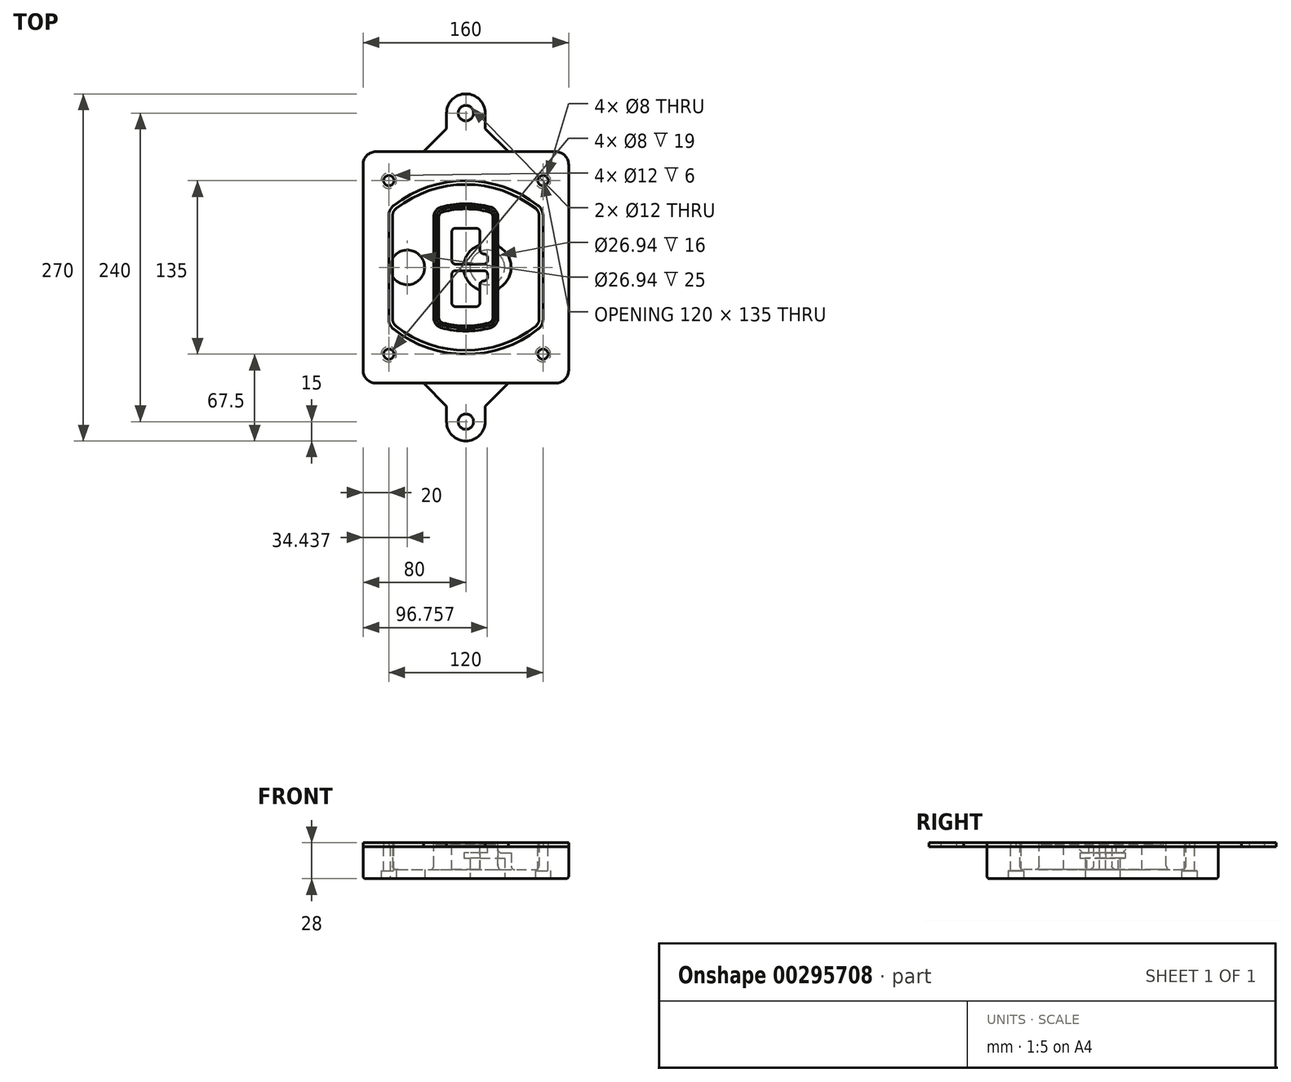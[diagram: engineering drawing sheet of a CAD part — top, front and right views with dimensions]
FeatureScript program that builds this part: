
annotation { "Feature Type Name" : "Feature", "Feature Type Description" : "" }
export const myFeature = defineFeature(function(context is Context, id is Id, definition is map)
    precondition{}
    {
        {
            var Q0;
            Q0=qCreatedBy(makeId("Top.planeOp"),FACE);
            var sketch = newSketch(context, id + "F0", { "sketchPlane" : qUnion([Q0])});
            skPoint(sketch, "E0.rect.middle", {"position": v(0, 0) * mm});
            skLineSegment(sketch, "E1.bottom", {"start": v(-70, -90) * mm, "end": v(70, -90) * mm});
            skLineSegment(sketch, "E1.top", {"start": v(-70, 90) * mm, "end": v(70, 90) * mm});
            skLineSegment(sketch, "E1.left", {"start": v(-80, -80) * mm, "end": v(-80, 80) * mm});
            skLineSegment(sketch, "E1.right", {"start": v(80, -80) * mm, "end": v(80, 80) * mm});
            skLineSegment(sketch, "E2", {"start": v(-80, 90) * mm, "end": v(80, -90) * mm, "construction": true});
            skLineSegment(sketch, "E3", {"start": v(80, 90) * mm, "end": v(-80, -90) * mm, "construction": true});
            skCircle(sketch, "E4", {"center": v(-60, 67.5) * mm, "radius": 4 * mm});
            skCircle(sketch, "E5", {"center": v(60, 67.5) * mm, "radius": 4 * mm});
            skCircle(sketch, "E6", {"center": v(60, -67.5) * mm, "radius": 4 * mm});
            skCircle(sketch, "E7", {"center": v(-60, -67.5) * mm, "radius": 4 * mm});
            skLineSegment(sketch, "E8", {"start": v(-60, 67.5) * mm, "end": v(60, 67.5) * mm, "construction": true});
            skLineSegment(sketch, "E9", {"start": v(60, 67.5) * mm, "end": v(60, -67.5) * mm, "construction": true});
            skLineSegment(sketch, "E10", {"start": v(60, -67.5) * mm, "end": v(-60, -67.5) * mm, "construction": true});
            skLineSegment(sketch, "E11", {"start": v(-60, -67.5) * mm, "end": v(-60, 67.5) * mm, "construction": true});
            skLineSegment(sketch, "E12", {"start": v(-60, 40.3) * mm, "end": v(-60, -40.3) * mm});
            skLineSegment(sketch, "E13", {"start": v(60, 40.3) * mm, "end": v(60, -40.3) * mm});
            skArc(sketch, "E14", {"start": v(56.15, 48.18) * mm, "mid": v(0, 67.5) * mm, "end": v(-56.15, 48.18) * mm});
            skArc(sketch, "E15", {"start": v(-56.15, -48.18) * mm, "mid": v(0, -67.5) * mm, "end": v(56.15, -48.18) * mm});
            skLineSegment(sketch, "E16", {"start": v(-60, 0) * mm, "end": v(60, 0) * mm, "construction": true});
            skPoint(sketch, "E17.visualSharp", {"position": v(-60, -45) * mm});
            skArc(sketch, "E17.filletArc", {"start": v(-60, -40.3) * mm, "mid": v(-58.99, -44.68) * mm, "end": v(-56.15, -48.18) * mm});
            skPoint(sketch, "E18.visualSharp", {"position": v(-60, 45) * mm});
            skArc(sketch, "E18.filletArc", {"start": v(-56.15, 48.18) * mm, "mid": v(-58.99, 44.68) * mm, "end": v(-60, 40.3) * mm});
            skPoint(sketch, "E19.visualSharp", {"position": v(60, 45) * mm});
            skArc(sketch, "E19.filletArc", {"start": v(60, 40.3) * mm, "mid": v(58.99, 44.68) * mm, "end": v(56.15, 48.18) * mm});
            skPoint(sketch, "E20.visualSharp", {"position": v(60, -45) * mm});
            skArc(sketch, "E20.filletArc", {"start": v(56.15, -48.18) * mm, "mid": v(58.99, -44.68) * mm, "end": v(60, -40.3) * mm});
            skPoint(sketch, "E21.visualSharp", {"position": v(-80, 90) * mm});
            skArc(sketch, "E21.filletArc", {"start": v(-70, 90) * mm, "mid": v(-77.07, 87.07) * mm, "end": v(-80, 80) * mm});
            skPoint(sketch, "E22.visualSharp", {"position": v(80, 90) * mm});
            skArc(sketch, "E22.filletArc", {"start": v(80, 80) * mm, "mid": v(77.07, 87.07) * mm, "end": v(70, 90) * mm});
            skPoint(sketch, "E23.visualSharp", {"position": v(80, -90) * mm});
            skArc(sketch, "E23.filletArc", {"start": v(70, -90) * mm, "mid": v(77.07, -87.07) * mm, "end": v(80, -80) * mm});
            skPoint(sketch, "E24.visualSharp", {"position": v(-80, -90) * mm});
            skArc(sketch, "E24.filletArc", {"start": v(-80, -80) * mm, "mid": v(-77.07, -87.07) * mm, "end": v(-70, -90) * mm});
            skArc(sketch, "E25.0", {"start": v(57, 40.3) * mm, "mid": v(56.3, 43.36) * mm, "end": v(54.3, 45.81) * mm});
            skLineSegment(sketch, "E25.1", {"start": v(57, 40.3) * mm, "end": v(57, -40.3) * mm});
            skArc(sketch, "E25.2", {"start": v(54.3, -45.81) * mm, "mid": v(56.3, -43.36) * mm, "end": v(57, -40.3) * mm});
            skArc(sketch, "E25.3", {"start": v(-54.3, -45.81) * mm, "mid": v(0, -64.5) * mm, "end": v(54.3, -45.81) * mm});
            skArc(sketch, "E25.4", {"start": v(-57, -40.3) * mm, "mid": v(-56.3, -43.36) * mm, "end": v(-54.3, -45.81) * mm});
            skArc(sketch, "E25.5", {"start": v(54.3, 45.81) * mm, "mid": v(0, 64.5) * mm, "end": v(-54.3, 45.81) * mm});
            skLineSegment(sketch, "E25.6", {"start": v(-57, 40.3) * mm, "end": v(-57, -40.3) * mm});
            skArc(sketch, "E25.7", {"start": v(-54.3, 45.81) * mm, "mid": v(-56.3, 43.36) * mm, "end": v(-57, 40.3) * mm});
            skArc(sketch, "E26.0", {"start": v(-58.62, 51.33) * mm, "mid": v(-62.58, 46.43) * mm, "end": v(-64, 40.3) * mm});
            skArc(sketch, "E26.1", {"start": v(58.62, 51.33) * mm, "mid": v(0, 71.5) * mm, "end": v(-58.62, 51.33) * mm});
            skArc(sketch, "E26.2", {"start": v(64, 40.3) * mm, "mid": v(62.58, 46.43) * mm, "end": v(58.62, 51.33) * mm});
            skLineSegment(sketch, "E26.3", {"start": v(64, 40.3) * mm, "end": v(64, -40.3) * mm});
            skArc(sketch, "E26.4", {"start": v(58.62, -51.33) * mm, "mid": v(62.58, -46.43) * mm, "end": v(64, -40.3) * mm});
            skLineSegment(sketch, "E26.5", {"start": v(-64, 40.3) * mm, "end": v(-64, -40.3) * mm});
            skArc(sketch, "E26.6", {"start": v(-58.62, -51.33) * mm, "mid": v(0, -71.5) * mm, "end": v(58.62, -51.33) * mm});
            skArc(sketch, "E26.7", {"start": v(-64, -40.3) * mm, "mid": v(-62.58, -46.43) * mm, "end": v(-58.62, -51.33) * mm});
            skSolve(sketch);
        }
        {
            var Q0;
            Q0=makeQuery(id+"F0.imprint","IMPRINT",FACE,{"disambiguationData":[TD([[makeQuery(id+"F0.imprint","IMPRINT",EDGE,{"derivedFrom":sQuery(id+"F0.wireOp",EDGE,"E1.bottom")}),1.0]])]});
            var Q1;
            Q1=makeQuery(id+"F0.imprint","IMPRINT",FACE,{"disambiguationData":[TD([[makeQuery(id+"F0.imprint","IMPRINT",EDGE,{"derivedFrom":sQuery(id+"F0.wireOp",EDGE,"E12")}),1.0]])]});
            var Q2;
            Q2=makeQuery(id+"F0.imprint","IMPRINT",FACE,{"disambiguationData":[TD([[makeQuery(id+"F0.imprint","IMPRINT",EDGE,{"derivedFrom":sQuery(id+"F0.wireOp",EDGE,"E25.0")}),1.0]])]});
            var Q3;
            Q3=makeQuery(id+"F0.imprint","IMPRINT",FACE,{"disambiguationData":[TD([[makeQuery(id+"F0.imprint","IMPRINT",EDGE,{"derivedFrom":sQuery(id+"F0.wireOp",EDGE,"E12")}),-1.0]])]});
            extrude(context, id + "F1", {"entities" : qUnion([Q0, Q1, Q2, Q3]), "oppositeDirection" : true, "depth" : 25 * mm});
        }
        {
            var Q0;
            Q0=makeQuery(id+"F0.imprint","IMPRINT",FACE,{"disambiguationData":[TD([[makeQuery(id+"F0.imprint","IMPRINT",EDGE,{"derivedFrom":sQuery(id+"F0.wireOp",EDGE,"E12")}),1.0]])]});
            extrude(context, id + "F2", {"entities" : qUnion([Q0]), "operationType" : NewBodyOperationType.ADD, "depth" : 3 * mm});
        }
        {
            var Q0;
            Q0=makeQuery(id+"F0.imprint","IMPRINT",FACE,{"disambiguationData":[TD([[makeQuery(id+"F0.imprint","IMPRINT",EDGE,{"derivedFrom":sQuery(id+"F0.wireOp",EDGE,"E25.0")}),1.0]])]});
            extrude(context, id + "F3", {"entities" : qUnion([Q0]), "operationType" : NewBodyOperationType.REMOVE, "oppositeDirection" : true, "depth" : 18 * mm});
        }
        {
            var Q0;
            Q0=makeQuery(id+"F2.opExtrude","CAP_FACE",FACE,{"disambiguationData":[OSD([sQuery(id+"F0.wireOp",EDGE,"E12"),sQuery(id+"F0.wireOp",EDGE,"E13"),sQuery(id+"F0.wireOp",EDGE,"E14"),sQuery(id+"F0.wireOp",EDGE,"E15"),sQuery(id+"F0.wireOp",EDGE,"E17.filletArc"),sQuery(id+"F0.wireOp",EDGE,"E18.filletArc"),sQuery(id+"F0.wireOp",EDGE,"E19.filletArc"),sQuery(id+"F0.wireOp",EDGE,"E20.filletArc"),sQuery(id+"F0.wireOp",EDGE,"E25.0"),sQuery(id+"F0.wireOp",EDGE,"E25.1"),sQuery(id+"F0.wireOp",EDGE,"E25.2"),sQuery(id+"F0.wireOp",EDGE,"E25.3"),sQuery(id+"F0.wireOp",EDGE,"E25.4"),sQuery(id+"F0.wireOp",EDGE,"E25.5"),sQuery(id+"F0.wireOp",EDGE,"E25.6"),sQuery(id+"F0.wireOp",EDGE,"E25.7")])],"isStart":false});
            var sketch = newSketch(context, id + "F4", { "sketchPlane" : qUnion([Q0])});
            skArc(sketch, "E27.0", {"start": v(-19.08, -46.97) * mm, "mid": v(0, -49.5) * mm, "end": v(19.08, -46.97) * mm});
            skArc(sketch, "E28.0", {"start": v(19.08, 46.97) * mm, "mid": v(0, 49.5) * mm, "end": v(-19.08, 46.97) * mm});
            skLineSegment(sketch, "E29", {"start": v(-25, 39.25) * mm, "end": v(-25, -39.25) * mm});
            skLineSegment(sketch, "E30", {"start": v(25, 39.25) * mm, "end": v(25, -39.25) * mm});
            skLineSegment(sketch, "E31", {"start": v(-25, 45.1) * mm, "end": v(25, 45.1) * mm, "construction": true});
            skLineSegment(sketch, "E32", {"start": v(-25, -45.1) * mm, "end": v(25, -45.1) * mm, "construction": true});
            skPoint(sketch, "E33.visualSharp", {"position": v(-25, 45.1) * mm});
            skArc(sketch, "E33.filletArc", {"start": v(-19.08, 46.97) * mm, "mid": v(-23.35, 44.11) * mm, "end": v(-25, 39.25) * mm});
            skPoint(sketch, "E34.visualSharp", {"position": v(25, 45.1) * mm});
            skArc(sketch, "E34.filletArc", {"start": v(25, 39.25) * mm, "mid": v(23.35, 44.11) * mm, "end": v(19.08, 46.97) * mm});
            skPoint(sketch, "E35.visualSharp", {"position": v(25, -45.1) * mm});
            skArc(sketch, "E35.filletArc", {"start": v(19.08, -46.97) * mm, "mid": v(23.35, -44.11) * mm, "end": v(25, -39.25) * mm});
            skPoint(sketch, "E36.visualSharp", {"position": v(-25, -45.1) * mm});
            skArc(sketch, "E36.filletArc", {"start": v(-25, -39.25) * mm, "mid": v(-23.35, -44.11) * mm, "end": v(-19.08, -46.97) * mm});
            skArc(sketch, "E37.0", {"start": v(54.3, 45.81) * mm, "mid": v(0, 64.5) * mm, "end": v(-54.3, 45.81) * mm});
            skArc(sketch, "E37.1", {"start": v(-54.3, 45.81) * mm, "mid": v(-56.3, 43.36) * mm, "end": v(-57, 40.3) * mm});
            skLineSegment(sketch, "E37.2", {"start": v(-57, 40.3) * mm, "end": v(-57, -40.3) * mm});
            skArc(sketch, "E37.3", {"start": v(-57, -40.3) * mm, "mid": v(-56.3, -43.36) * mm, "end": v(-54.3, -45.81) * mm});
            skArc(sketch, "E37.4", {"start": v(-54.3, -45.81) * mm, "mid": v(0, -64.5) * mm, "end": v(54.3, -45.81) * mm});
            skArc(sketch, "E37.5", {"start": v(54.3, -45.81) * mm, "mid": v(56.3, -43.36) * mm, "end": v(57, -40.3) * mm});
            skLineSegment(sketch, "E37.6", {"start": v(57, 40.3) * mm, "end": v(57, -40.3) * mm});
            skArc(sketch, "E37.7", {"start": v(57, 40.3) * mm, "mid": v(56.3, 43.36) * mm, "end": v(54.3, 45.81) * mm});
            skLineSegment(sketch, "E38.0", {"start": v(23, 39.25) * mm, "end": v(23, -39.25) * mm});
            skArc(sketch, "E38.1", {"start": v(18.56, -45.04) * mm, "mid": v(21.76, -42.9) * mm, "end": v(23, -39.25) * mm});
            skArc(sketch, "E38.2", {"start": v(-18.56, -45.04) * mm, "mid": v(0, -47.5) * mm, "end": v(18.56, -45.04) * mm});
            skArc(sketch, "E38.3", {"start": v(-23, -39.25) * mm, "mid": v(-21.76, -42.9) * mm, "end": v(-18.56, -45.04) * mm});
            skLineSegment(sketch, "E38.4", {"start": v(-23, 39.25) * mm, "end": v(-23, -39.25) * mm});
            skArc(sketch, "E38.5", {"start": v(23, 39.25) * mm, "mid": v(21.76, 42.9) * mm, "end": v(18.56, 45.04) * mm});
            skArc(sketch, "E38.6", {"start": v(-18.56, 45.04) * mm, "mid": v(-21.76, 42.9) * mm, "end": v(-23, 39.25) * mm});
            skArc(sketch, "E38.7", {"start": v(18.56, 45.04) * mm, "mid": v(0, 47.5) * mm, "end": v(-18.56, 45.04) * mm});
            skArc(sketch, "E39.0", {"start": v(21, 39.25) * mm, "mid": v(20.18, 41.68) * mm, "end": v(18.04, 43.1) * mm});
            skLineSegment(sketch, "E39.1", {"start": v(21, 39.25) * mm, "end": v(21, -39.25) * mm});
            skArc(sketch, "E39.2", {"start": v(18.04, -43.1) * mm, "mid": v(20.18, -41.68) * mm, "end": v(21, -39.25) * mm});
            skArc(sketch, "E39.3", {"start": v(-18.04, -43.1) * mm, "mid": v(0, -45.5) * mm, "end": v(18.04, -43.1) * mm});
            skArc(sketch, "E39.4", {"start": v(-21, -39.25) * mm, "mid": v(-20.18, -41.68) * mm, "end": v(-18.04, -43.1) * mm});
            skArc(sketch, "E39.5", {"start": v(18.04, 43.1) * mm, "mid": v(0, 45.5) * mm, "end": v(-18.04, 43.1) * mm});
            skLineSegment(sketch, "E39.6", {"start": v(-21, 39.25) * mm, "end": v(-21, -39.25) * mm});
            skArc(sketch, "E39.7", {"start": v(-18.04, 43.1) * mm, "mid": v(-20.18, 41.68) * mm, "end": v(-21, 39.25) * mm});
            skLineSegment(sketch, "E40", {"start": v(-25, 0) * mm, "end": v(25, 0) * mm, "construction": true});
            skLineSegment(sketch, "E41", {"start": v(-11, 5.5) * mm, "end": v(-11, 27.5) * mm});
            skLineSegment(sketch, "E42", {"start": v(-8, 30.5) * mm, "end": v(8, 30.5) * mm});
            skLineSegment(sketch, "E43", {"start": v(11, 27.5) * mm, "end": v(11, 13.5) * mm});
            skLineSegment(sketch, "E44", {"start": v(14, 10.5) * mm, "end": v(14, 10.5) * mm});
            skLineSegment(sketch, "E45", {"start": v(17, 7.5) * mm, "end": v(17, 5.5) * mm});
            skLineSegment(sketch, "E46", {"start": v(14, 2.5) * mm, "end": v(-8, 2.5) * mm});
            skPoint(sketch, "E47.visualSharp", {"position": v(-11, 30.5) * mm});
            skArc(sketch, "E47.filletArc", {"start": v(-8, 30.5) * mm, "mid": v(-10.12, 29.62) * mm, "end": v(-11, 27.5) * mm});
            skPoint(sketch, "E48.visualSharp", {"position": v(11, 30.5) * mm});
            skArc(sketch, "E48.filletArc", {"start": v(11, 27.5) * mm, "mid": v(10.12, 29.62) * mm, "end": v(8, 30.5) * mm});
            skPoint(sketch, "E49.visualSharp", {"position": v(11, 10.5) * mm});
            skArc(sketch, "E49.filletArc", {"start": v(11, 13.5) * mm, "mid": v(11.88, 11.38) * mm, "end": v(14, 10.5) * mm});
            skPoint(sketch, "E50.visualSharp", {"position": v(17, 10.5) * mm});
            skArc(sketch, "E50.filletArc", {"start": v(17, 7.5) * mm, "mid": v(16.12, 9.62) * mm, "end": v(14, 10.5) * mm});
            skPoint(sketch, "E51.visualSharp", {"position": v(17, 2.5) * mm});
            skArc(sketch, "E51.filletArc", {"start": v(14, 2.5) * mm, "mid": v(16.12, 3.38) * mm, "end": v(17, 5.5) * mm});
            skPoint(sketch, "E52.visualSharp", {"position": v(-11, 2.5) * mm});
            skArc(sketch, "E52.filletArc", {"start": v(-11, 5.5) * mm, "mid": v(-10.12, 3.38) * mm, "end": v(-8, 2.5) * mm});
            skLineSegment(sketch, "E53.0.MirrorCS", {"start": v(14, -2.5) * mm, "end": v(-8, -2.5) * mm});
            skArc(sketch, "E54.0.MirrorCS", {"start": v(-11, -5.5) * mm, "mid": v(-10.12, -3.38) * mm, "end": v(-8, -2.5) * mm});
            skLineSegment(sketch, "E55.0.MirrorCS", {"start": v(-11, -5.5) * mm, "end": v(-11, -27.5) * mm});
            skArc(sketch, "E56.0.MirrorCS", {"start": v(-8, -30.5) * mm, "mid": v(-10.12, -29.62) * mm, "end": v(-11, -27.5) * mm});
            skLineSegment(sketch, "E57.0.MirrorCS", {"start": v(-8, -30.5) * mm, "end": v(8, -30.5) * mm});
            skArc(sketch, "E58.0.MirrorCS", {"start": v(11, -27.5) * mm, "mid": v(10.12, -29.62) * mm, "end": v(8, -30.5) * mm});
            skLineSegment(sketch, "E59.0.MirrorCS", {"start": v(11, -27.5) * mm, "end": v(11, -13.5) * mm});
            skArc(sketch, "E60.0.MirrorCS", {"start": v(11, -13.5) * mm, "mid": v(11.88, -11.38) * mm, "end": v(14, -10.5) * mm});
            skArc(sketch, "E61.0.MirrorCS", {"start": v(17, -7.5) * mm, "mid": v(16.12, -9.62) * mm, "end": v(14, -10.5) * mm});
            skLineSegment(sketch, "E62.0.MirrorCS", {"start": v(17, -7.5) * mm, "end": v(17, -5.5) * mm});
            skArc(sketch, "E63.0.MirrorCS", {"start": v(14, -2.5) * mm, "mid": v(16.12, -3.38) * mm, "end": v(17, -5.5) * mm});
            skSolve(sketch);
        }
        {
            var Q0;
            Q0=makeQuery(id+"F4.imprint","IMPRINT",FACE,{"disambiguationData":[TD([[makeQuery(id+"F4.imprint","IMPRINT",EDGE,{"derivedFrom":sQuery(id+"F4.wireOp",EDGE,"E27.0")}),1.0]])]});
            var Q1;
            Q1=makeQuery(id+"F4.imprint","IMPRINT",FACE,{"disambiguationData":[TD([[makeQuery(id+"F4.imprint","IMPRINT",EDGE,{"derivedFrom":sQuery(id+"F4.wireOp",EDGE,"E38.0")}),-1.0]])]});
            var Q2;
            Q2=makeQuery(id+"F4.imprint","IMPRINT",FACE,{"disambiguationData":[TD([[makeQuery(id+"F4.imprint","IMPRINT",EDGE,{"derivedFrom":sQuery(id+"F4.wireOp",EDGE,"E39.0")}),1.0]])]});
            extrude(context, id + "F5", {"entities" : qUnion([Q0, Q1, Q2]), "operationType" : NewBodyOperationType.ADD, "endBound" : BoundingType.UP_TO_NEXT, "oppositeDirection" : true, "depth" : 25 * mm});
        }
        {
            var Q0;
            Q0=makeQuery(id+"F4.imprint","IMPRINT",FACE,{"disambiguationData":[TD([[makeQuery(id+"F4.imprint","IMPRINT",EDGE,{"derivedFrom":sQuery(id+"F4.wireOp",EDGE,"E38.0")}),-1.0]])]});
            extrude(context, id + "F6", {"entities" : qUnion([Q0]), "operationType" : NewBodyOperationType.REMOVE, "oppositeDirection" : true, "depth" : 2 * mm});
        }
        {
            var Q0;
            Q0=makeQuery(id+"F1.opExtrude","CAP_FACE",FACE,{"disambiguationData":[OSD([sQuery(id+"F0.wireOp",EDGE,"E1.bottom"),sQuery(id+"F0.wireOp",EDGE,"E1.top"),sQuery(id+"F0.wireOp",EDGE,"E1.left"),sQuery(id+"F0.wireOp",EDGE,"E1.right"),sQuery(id+"F0.wireOp",EDGE,"E4"),sQuery(id+"F0.wireOp",EDGE,"E5"),sQuery(id+"F0.wireOp",EDGE,"E6"),sQuery(id+"F0.wireOp",EDGE,"E7"),sQuery(id+"F0.wireOp",EDGE,"E21.filletArc"),sQuery(id+"F0.wireOp",EDGE,"E22.filletArc"),sQuery(id+"F0.wireOp",EDGE,"E23.filletArc"),sQuery(id+"F0.wireOp",EDGE,"E24.filletArc")])],"isStart":false});
            var sketch = newSketch(context, id + "F7", { "sketchPlane" : qUnion([Q0])});
            skCircle(sketch, "E64", {"center": v(16.76, 0) * mm, "radius": 13.47 * mm});
            skCircle(sketch, "E65", {"center": v(-45.56, 0) * mm, "radius": 13.47 * mm});
            skLineSegment(sketch, "E66", {"start": v(80, 0) * mm, "end": v(-80, 0) * mm});
            skCircle(sketch, "E67", {"center": v(16.76, 0) * mm, "radius": 18.47 * mm});
            skCircle(sketch, "E68", {"center": v(60, -67.5) * mm, "radius": 6 * mm});
            skCircle(sketch, "E69", {"center": v(-60, -67.5) * mm, "radius": 6 * mm});
            skCircle(sketch, "E70", {"center": v(-60, 67.5) * mm, "radius": 6 * mm});
            skCircle(sketch, "E71", {"center": v(60, 67.5) * mm, "radius": 6 * mm});
            skSolve(sketch);
        }
        {
            var Q0;
            {var subQ1=sQuery(id+"F7.wireOp",EDGE,"E66");var subQ4=sQuery(id+"F7.wireOp",EDGE,"E64");var subQ6=makeQuery(id+"F7.imprint","INTERSECT",VERTEX,{"disambiguationData":[OD(0.0)],"derivedFrom":[subQ4,subQ1]});Q0=makeQuery(id+"F7.imprint","IMPRINT",FACE,{"disambiguationData":[TD([[makeQuery(id+"F7.imprint","IMPRINT",EDGE,{"disambiguationData":[TD([[subQ6,-1.0]])],"derivedFrom":subQ4}),-1.0]])]});}
            var Q1;
            {var subQ0=sQuery(id+"F7.wireOp",EDGE,"E66");var subQ1=sQuery(id+"F7.wireOp",EDGE,"E64");var subQ3=makeQuery(id+"F7.imprint","INTERSECT",VERTEX,{"disambiguationData":[OD(0.0)],"derivedFrom":[subQ1,subQ0]});Q1=makeQuery(id+"F7.imprint","IMPRINT",FACE,{"disambiguationData":[TD([[makeQuery(id+"F7.imprint","IMPRINT",EDGE,{"disambiguationData":[TD([[subQ3,-1.0]])],"derivedFrom":subQ1}),1.0]])]});}
            var Q2;
            {var subQ0=sQuery(id+"F7.wireOp",EDGE,"E66");var subQ1=sQuery(id+"F7.wireOp",EDGE,"E64");var subQ3=makeQuery(id+"F7.imprint","INTERSECT",VERTEX,{"disambiguationData":[OD(0.0)],"derivedFrom":[subQ1,subQ0]});Q2=makeQuery(id+"F7.imprint","IMPRINT",FACE,{"disambiguationData":[TD([[makeQuery(id+"F7.imprint","IMPRINT",EDGE,{"disambiguationData":[TD([[subQ3,1.0]])],"derivedFrom":subQ1}),1.0]])]});}
            var Q3;
            {var subQ1=sQuery(id+"F7.wireOp",EDGE,"E66");var subQ4=sQuery(id+"F7.wireOp",EDGE,"E64");var subQ6=makeQuery(id+"F7.imprint","INTERSECT",VERTEX,{"disambiguationData":[OD(0.0)],"derivedFrom":[subQ4,subQ1]});Q3=makeQuery(id+"F7.imprint","IMPRINT",FACE,{"disambiguationData":[TD([[makeQuery(id+"F7.imprint","IMPRINT",EDGE,{"disambiguationData":[TD([[subQ6,1.0]])],"derivedFrom":subQ4}),-1.0]])]});}
            extrude(context, id + "F8", {"entities" : qUnion([Q0, Q1, Q2, Q3]), "operationType" : NewBodyOperationType.ADD, "oppositeDirection" : true, "depth" : 20 * mm});
        }
        {
            var Q0;
            {var subQ0=sQuery(id+"F7.wireOp",EDGE,"E66");var subQ1=sQuery(id+"F7.wireOp",EDGE,"E64");var subQ3=makeQuery(id+"F7.imprint","INTERSECT",VERTEX,{"disambiguationData":[OD(0.0)],"derivedFrom":[subQ1,subQ0]});Q0=makeQuery(id+"F7.imprint","IMPRINT",FACE,{"disambiguationData":[TD([[makeQuery(id+"F7.imprint","IMPRINT",EDGE,{"disambiguationData":[TD([[subQ3,-1.0]])],"derivedFrom":subQ1}),1.0]])]});}
            var Q1;
            {var subQ0=sQuery(id+"F7.wireOp",EDGE,"E66");var subQ1=sQuery(id+"F7.wireOp",EDGE,"E64");var subQ3=makeQuery(id+"F7.imprint","INTERSECT",VERTEX,{"disambiguationData":[OD(0.0)],"derivedFrom":[subQ1,subQ0]});Q1=makeQuery(id+"F7.imprint","IMPRINT",FACE,{"disambiguationData":[TD([[makeQuery(id+"F7.imprint","IMPRINT",EDGE,{"disambiguationData":[TD([[subQ3,1.0]])],"derivedFrom":subQ1}),1.0]])]});}
            extrude(context, id + "F9", {"entities" : qUnion([Q0, Q1]), "operationType" : NewBodyOperationType.REMOVE, "oppositeDirection" : true, "depth" : 16 * mm});
        }
        {
            var Q0;
            {var subQ0=sQuery(id+"F7.wireOp",EDGE,"E66");var subQ1=sQuery(id+"F7.wireOp",EDGE,"E65");var subQ3=makeQuery(id+"F7.imprint","INTERSECT",VERTEX,{"disambiguationData":[OD(0.0)],"derivedFrom":[subQ1,subQ0]});Q0=makeQuery(id+"F7.imprint","IMPRINT",FACE,{"disambiguationData":[TD([[makeQuery(id+"F7.imprint","IMPRINT",EDGE,{"disambiguationData":[TD([[subQ3,-1.0]])],"derivedFrom":subQ1}),1.0]])]});}
            var Q1;
            {var subQ0=sQuery(id+"F7.wireOp",EDGE,"E66");var subQ1=sQuery(id+"F7.wireOp",EDGE,"E65");var subQ3=makeQuery(id+"F7.imprint","INTERSECT",VERTEX,{"disambiguationData":[OD(0.0)],"derivedFrom":[subQ1,subQ0]});Q1=makeQuery(id+"F7.imprint","IMPRINT",FACE,{"disambiguationData":[TD([[makeQuery(id+"F7.imprint","IMPRINT",EDGE,{"disambiguationData":[TD([[subQ3,1.0]])],"derivedFrom":subQ1}),1.0]])]});}
            extrude(context, id + "F10", {"entities" : qUnion([Q0, Q1]), "operationType" : NewBodyOperationType.REMOVE, "oppositeDirection" : true, "depth" : 25 * mm});
        }
        {
            var Q0;
            Q0=makeQuery(id+"F7.imprint","IMPRINT",FACE,{"disambiguationData":[TD([[makeQuery(id+"F7.imprint","IMPRINT",EDGE,{"derivedFrom":sQuery(id+"F7.wireOp",EDGE,"E68")}),1.0]])]});
            var Q1;
            Q1=makeQuery(id+"F7.imprint","IMPRINT",FACE,{"disambiguationData":[TD([[makeQuery(id+"F7.imprint","IMPRINT",EDGE,{"derivedFrom":makeQuery(id+"F1.opExtrude","CAP_EDGE",EDGE,{"disambiguationData":[OSD([sQuery(id+"F0.wireOp",EDGE,"E5")])],"isStart":false})}),-1.0]])]});
            var Q2;
            Q2=makeQuery(id+"F7.imprint","IMPRINT",FACE,{"disambiguationData":[TD([[makeQuery(id+"F7.imprint","IMPRINT",EDGE,{"derivedFrom":sQuery(id+"F7.wireOp",EDGE,"E69")}),1.0]])]});
            var Q3;
            Q3=makeQuery(id+"F7.imprint","IMPRINT",FACE,{"disambiguationData":[TD([[makeQuery(id+"F7.imprint","IMPRINT",EDGE,{"derivedFrom":makeQuery(id+"F1.opExtrude","CAP_EDGE",EDGE,{"disambiguationData":[OSD([sQuery(id+"F0.wireOp",EDGE,"E4")])],"isStart":false})}),-1.0]])]});
            var Q4;
            Q4=makeQuery(id+"F7.imprint","IMPRINT",FACE,{"disambiguationData":[TD([[makeQuery(id+"F7.imprint","IMPRINT",EDGE,{"derivedFrom":sQuery(id+"F7.wireOp",EDGE,"E70")}),1.0]])]});
            var Q5;
            Q5=makeQuery(id+"F7.imprint","IMPRINT",FACE,{"disambiguationData":[TD([[makeQuery(id+"F7.imprint","IMPRINT",EDGE,{"derivedFrom":makeQuery(id+"F1.opExtrude","CAP_EDGE",EDGE,{"disambiguationData":[OSD([sQuery(id+"F0.wireOp",EDGE,"E7")])],"isStart":false})}),-1.0]])]});
            var Q6;
            Q6=makeQuery(id+"F7.imprint","IMPRINT",FACE,{"disambiguationData":[TD([[makeQuery(id+"F7.imprint","IMPRINT",EDGE,{"derivedFrom":sQuery(id+"F7.wireOp",EDGE,"E71")}),1.0]])]});
            var Q7;
            Q7=makeQuery(id+"F7.imprint","IMPRINT",FACE,{"disambiguationData":[TD([[makeQuery(id+"F7.imprint","IMPRINT",EDGE,{"derivedFrom":makeQuery(id+"F1.opExtrude","CAP_EDGE",EDGE,{"disambiguationData":[OSD([sQuery(id+"F0.wireOp",EDGE,"E6")])],"isStart":false})}),-1.0]])]});
            extrude(context, id + "F11", {"entities" : qUnion([Q0, Q1, Q2, Q3, Q4, Q5, Q6, Q7]), "operationType" : NewBodyOperationType.REMOVE, "oppositeDirection" : true, "depth" : 6 * mm});
        }
        {
            var Q0;
            Q0=makeQuery(id+"F9.boolean.opBoolean","COPY",FACE,{"derivedFrom":makeQuery(id+"F9.opExtrude","CAP_FACE",FACE,{"disambiguationData":[OSD([sQuery(id+"F7.wireOp",EDGE,"E64")])],"isStart":false})});
            var sketch = newSketch(context, id + "F12", { "sketchPlane" : qUnion([Q0])});
            skArc(sketch, "E72.0", {"start": v(11, 17.55) * mm, "mid": v(2.57, 11.82) * mm, "end": v(-1.54, 2.5) * mm});
            skArc(sketch, "E72.1", {"start": v(-1.54, -2.5) * mm, "mid": v(2.57, -11.82) * mm, "end": v(11, -17.55) * mm});
            skLineSegment(sketch, "E73", {"start": v(-1.54, -2.5) * mm, "end": v(14, -2.5) * mm});
            skLineSegment(sketch, "E74.0", {"start": v(14, 2.5) * mm, "end": v(-1.54, 2.5) * mm});
            skArc(sketch, "E74.1", {"start": v(14, 2.5) * mm, "mid": v(16.12, 3.38) * mm, "end": v(17, 5.5) * mm});
            skLineSegment(sketch, "E74.2", {"start": v(17, 7.5) * mm, "end": v(17, 5.5) * mm});
            skArc(sketch, "E74.3", {"start": v(17, 7.5) * mm, "mid": v(16.12, 9.62) * mm, "end": v(14, 10.5) * mm});
            skArc(sketch, "E74.4", {"start": v(11, 13.5) * mm, "mid": v(11.88, 11.38) * mm, "end": v(14, 10.5) * mm});
            skLineSegment(sketch, "E74.5", {"start": v(11, 17.55) * mm, "end": v(11, 13.5) * mm});
            skLineSegment(sketch, "E74.7", {"start": v(14, -2.5) * mm, "end": v(-1.54, -2.5) * mm});
            skArc(sketch, "E74.8", {"start": v(14, -2.5) * mm, "mid": v(16.12, -3.38) * mm, "end": v(17, -5.5) * mm});
            skLineSegment(sketch, "E74.9", {"start": v(17, -7.5) * mm, "end": v(17, -5.5) * mm});
            skArc(sketch, "E74.10", {"start": v(17, -7.5) * mm, "mid": v(16.12, -9.62) * mm, "end": v(14, -10.5) * mm});
            skArc(sketch, "E74.11", {"start": v(11, -13.5) * mm, "mid": v(11.88, -11.38) * mm, "end": v(14, -10.5) * mm});
            skLineSegment(sketch, "E74.12", {"start": v(11, -17.55) * mm, "end": v(11, -13.5) * mm});
            skPoint(sketch, "E75.orphan", {"position": v(11, -27.5) * mm});
            skPoint(sketch, "E76.orphan", {"position": v(-8, -2.5) * mm});
            skPoint(sketch, "E77.orphan", {"position": v(-8, 2.5) * mm});
            skPoint(sketch, "E78.orphan", {"position": v(11, 27.5) * mm});
            skSolve(sketch);
        }
        {
            var Q0;
            {var subQ7=sQuery(id+"F12.wireOp",EDGE,"E72.0");var subQ14=sQuery(id+"F12.wireOp",EDGE,"E72.1");var subQ16=sQuery(id+"F12.wireOp",EDGE,"E74.1");var subQ18=sQuery(id+"F12.wireOp",EDGE,"E74.8");Q0=qUnion([makeQuery(id+"F12.imprint","IMPRINT",FACE,{"disambiguationData":[TD([[makeQuery(id+"F12.imprint","IMPRINT",EDGE,{"derivedFrom":subQ7}),1.0]])]}),makeQuery(id+"F12.imprint","IMPRINT",FACE,{"disambiguationData":[TD([[makeQuery(id+"F12.imprint","IMPRINT",EDGE,{"derivedFrom":subQ14}),1.0]])]}),makeQuery(id+"F12.imprint","IMPRINT",FACE,{"disambiguationData":[TD([[makeQuery(id+"F12.imprint","IMPRINT",EDGE,{"derivedFrom":subQ16}),1.0]])]}),makeQuery(id+"F12.imprint","IMPRINT",FACE,{"disambiguationData":[TD([[makeQuery(id+"F12.imprint","IMPRINT",EDGE,{"derivedFrom":subQ18}),-1.0]])]})]);}
            var Q1;
            Q1=makeQuery(id+"F5.boolean.opBoolean","SPLIT",FACE,{"disambiguationData":[TD([makeQuery(id+"F5.opExtrude","SWEPT_FACE",FACE,{"disambiguationData":[OSD([sQuery(id+"F4.wireOp",EDGE,"E41")])]})])],"derivedFrom":makeQuery(id+"F3.boolean.opBoolean","COPY",FACE,{"derivedFrom":makeQuery(id+"F3.opExtrude","CAP_FACE",FACE,{"disambiguationData":[OSD([sQuery(id+"F0.wireOp",EDGE,"E25.0"),sQuery(id+"F0.wireOp",EDGE,"E25.1"),sQuery(id+"F0.wireOp",EDGE,"E25.2"),sQuery(id+"F0.wireOp",EDGE,"E25.3"),sQuery(id+"F0.wireOp",EDGE,"E25.4"),sQuery(id+"F0.wireOp",EDGE,"E25.5"),sQuery(id+"F0.wireOp",EDGE,"E25.6"),sQuery(id+"F0.wireOp",EDGE,"E25.7")])],"isStart":false})})});
            extrude(context, id + "F13", {"entities" : qUnion([Q0]), "operationType" : NewBodyOperationType.REMOVE, "endBound" : BoundingType.UP_TO_SURFACE, "endBoundEntityFace" : qUnion([Q1]), "depth" : 25 * mm});
        }
        {
            var Q0;
            Q0=makeQuery(id+"F3.boolean.opBoolean","COPY",EDGE,{"derivedFrom":makeQuery(id+"F3.opExtrude","CAP_EDGE",EDGE,{"disambiguationData":[OSD([sQuery(id+"F0.wireOp",EDGE,"E25.6")])],"isStart":false})});
            var Q1;
            Q1=makeQuery(id+"F8.boolean.opBoolean","INTERSECT",EDGE,{"derivedFrom":[makeQuery(id+"F5.opExtrude","SWEPT_FACE",FACE,{"disambiguationData":[OSD([sQuery(id+"F4.wireOp",EDGE,"E30")])]}),makeQuery(id+"F8.opExtrude","CAP_FACE",FACE,{"disambiguationData":[OSD([sQuery(id+"F7.wireOp",EDGE,"E67")])],"isStart":false})]});
            var Q2;
            Q2=makeQuery(id+"F8.boolean.opBoolean","INTERSECT",EDGE,{"disambiguationData":[OD(1.0)],"derivedFrom":[makeQuery(id+"F5.opExtrude","SWEPT_FACE",FACE,{"disambiguationData":[OSD([sQuery(id+"F4.wireOp",EDGE,"E30")])]}),makeQuery(id+"F8.opExtrude","SWEPT_FACE",FACE,{"disambiguationData":[OSD([sQuery(id+"F7.wireOp",EDGE,"E67")])]})]});
            var Q3;
            {var subQ0=sQuery(id+"F4.wireOp",EDGE,"E30");Q3=makeQuery(id+"F8.boolean.opBoolean","SPLIT",EDGE,{"disambiguationData":[TD([makeQuery(id+"F5.opExtrude","SWEPT_FACE",FACE,{"disambiguationData":[OSD([sQuery(id+"F4.wireOp",EDGE,"E35.filletArc")])]})])],"derivedFrom":makeQuery(id+"F5.opExtrude","CAP_EDGE",EDGE,{"disambiguationData":[OSD([subQ0])],"isStart":false})});}
            var Q4;
            {var subQ0=sQuery(id+"F0.wireOp",EDGE,"E25.7");var subQ1=sQuery(id+"F0.wireOp",EDGE,"E25.1");var subQ2=sQuery(id+"F0.wireOp",EDGE,"E25.6");var subQ3=sQuery(id+"F0.wireOp",EDGE,"E25.5");var subQ4=sQuery(id+"F0.wireOp",EDGE,"E25.4");var subQ5=sQuery(id+"F0.wireOp",EDGE,"E25.0");var subQ6=sQuery(id+"F0.wireOp",EDGE,"E25.2");var subQ7=sQuery(id+"F0.wireOp",EDGE,"E25.3");Q4=makeQuery(id+"F8.boolean.opBoolean","INTERSECT",EDGE,{"derivedFrom":[makeQuery(id+"F5.boolean.opBoolean","SPLIT",FACE,{"disambiguationData":[TD([makeQuery(id+"F2.opExtrude","SWEPT_FACE",FACE,{"disambiguationData":[OSD([subQ5])]})])],"derivedFrom":makeQuery(id+"F3.boolean.opBoolean","COPY",FACE,{"derivedFrom":makeQuery(id+"F3.opExtrude","CAP_FACE",FACE,{"disambiguationData":[OSD([subQ5,subQ1,subQ6,subQ7,subQ4,subQ3,subQ2,subQ0])],"isStart":false})})}),makeQuery(id+"F8.opExtrude","SWEPT_FACE",FACE,{"disambiguationData":[OSD([sQuery(id+"F7.wireOp",EDGE,"E67")])]})]});}
            var Q5;
            Q5=makeQuery(id+"F8.boolean.opBoolean","INTERSECT",EDGE,{"disambiguationData":[OD(0.0)],"derivedFrom":[makeQuery(id+"F5.opExtrude","SWEPT_FACE",FACE,{"disambiguationData":[OSD([sQuery(id+"F4.wireOp",EDGE,"E30")])]}),makeQuery(id+"F8.opExtrude","SWEPT_FACE",FACE,{"disambiguationData":[OSD([sQuery(id+"F7.wireOp",EDGE,"E67")])]})]});
            fillet(context, id + "F14", {"entities" : qUnion([Q0, Q1, Q2, Q3, Q4, Q5]), "radius" : 3 * mm, "tangentPropagation" : true, "allowEdgeOverflow" : false});
        }
        {
            var Q0;
            Q0=makeQuery(id+"F1.opExtrude","CAP_EDGE",EDGE,{"disambiguationData":[OSD([sQuery(id+"F0.wireOp",EDGE,"E1.bottom")])],"isStart":false});
            fillet(context, id + "F15", {"entities" : qUnion([Q0]), "radius" : 2 * mm, "tangentPropagation" : true, "allowEdgeOverflow" : false});
        }
        {
            var Q0;
            {var subQ0=sQuery(id+"F0.wireOp",EDGE,"E21.filletArc");var subQ1=sQuery(id+"F0.wireOp",EDGE,"E7");var subQ2=sQuery(id+"F0.wireOp",EDGE,"E6");var subQ3=sQuery(id+"F0.wireOp",EDGE,"E5");var subQ4=sQuery(id+"F0.wireOp",EDGE,"E4");var subQ5=sQuery(id+"F0.wireOp",EDGE,"E22.filletArc");var subQ6=sQuery(id+"F0.wireOp",EDGE,"E1.bottom");var subQ7=sQuery(id+"F0.wireOp",EDGE,"E1.right");var subQ8=sQuery(id+"F0.wireOp",EDGE,"E1.top");var subQ9=sQuery(id+"F0.wireOp",EDGE,"E1.left");var subQ10=sQuery(id+"F0.wireOp",EDGE,"E23.filletArc");var subQ11=sQuery(id+"F0.wireOp",EDGE,"E24.filletArc");Q0=makeQuery(id+"F2.boolean.opBoolean","SPLIT",FACE,{"disambiguationData":[TD([makeQuery(id+"F1.opExtrude","SWEPT_FACE",FACE,{"disambiguationData":[OSD([subQ6])]})])],"derivedFrom":makeQuery(id+"F1.opExtrude","CAP_FACE",FACE,{"disambiguationData":[OSD([subQ6,subQ8,subQ9,subQ7,subQ4,subQ3,subQ2,subQ1,subQ0,subQ5,subQ10,subQ11])],"isStart":true})});}
            var sketch = newSketch(context, id + "F16", { "sketchPlane" : qUnion([Q0])});
            skLineSegment(sketch, "E79", {"start": v(0, 90) * mm, "end": v(0, 120) * mm, "construction": true});
            skCircle(sketch, "E80", {"center": v(0, 120) * mm, "radius": 6 * mm});
            skLineSegment(sketch, "E81", {"start": v(-33, 90) * mm, "end": v(-15, 108) * mm});
            skLineSegment(sketch, "E82", {"start": v(-15, 108) * mm, "end": v(-15, 120) * mm});
            skLineSegment(sketch, "E83.MirrorCS", {"start": v(15, 108) * mm, "end": v(15, 120) * mm});
            skLineSegment(sketch, "E84.MirrorCS", {"start": v(33, 90) * mm, "end": v(15, 108) * mm});
            skArc(sketch, "E85", {"start": v(15, 120) * mm, "mid": v(0, 135) * mm, "end": v(-15, 120) * mm});
            skLineSegment(sketch, "E86", {"start": v(-80, 0) * mm, "end": v(80, 0) * mm, "construction": true});
            skLineSegment(sketch, "E87.MirrorCS", {"start": v(33, -90) * mm, "end": v(15, -108) * mm});
            skLineSegment(sketch, "E88.MirrorCS", {"start": v(-33, -90) * mm, "end": v(-15, -108) * mm});
            skLineSegment(sketch, "E89.MirrorCS", {"start": v(-15, -108) * mm, "end": v(-15, -120) * mm});
            skLineSegment(sketch, "E90.MirrorCS", {"start": v(15, -108) * mm, "end": v(15, -120) * mm});
            skCircle(sketch, "E91.MirrorC", {"center": v(0, -120) * mm, "radius": 6 * mm});
            skArc(sketch, "E92.MirrorCS", {"start": v(15, -120) * mm, "mid": v(0, -135) * mm, "end": v(-15, -120) * mm});
            skLineSegment(sketch, "E93.MirrorCS", {"start": v(0, -90) * mm, "end": v(0, -120) * mm, "construction": true});
            skSolve(sketch);
        }
        {
            var Q0;
            Q0=makeQuery(id+"F16.imprint","IMPRINT",FACE,{"disambiguationData":[TD([[makeQuery(id+"F16.imprint","IMPRINT",EDGE,{"derivedFrom":sQuery(id+"F16.wireOp",EDGE,"E80")}),-1.0]])]});
            var Q1;
            {var subQ1=sQuery(id+"F16.wireOp",EDGE,"E87.MirrorCS");Q1=makeQuery(id+"F16.imprint","IMPRINT",FACE,{"disambiguationData":[TD([[makeQuery(id+"F16.imprint","IMPRINT",EDGE,{"derivedFrom":subQ1}),-1.0]])]});}
            var Q2;
            Q2=makeQuery(id+"F2.opExtrude","CAP_FACE",FACE,{"disambiguationData":[OSD([sQuery(id+"F0.wireOp",EDGE,"E12"),sQuery(id+"F0.wireOp",EDGE,"E13"),sQuery(id+"F0.wireOp",EDGE,"E14"),sQuery(id+"F0.wireOp",EDGE,"E15"),sQuery(id+"F0.wireOp",EDGE,"E17.filletArc"),sQuery(id+"F0.wireOp",EDGE,"E18.filletArc"),sQuery(id+"F0.wireOp",EDGE,"E19.filletArc"),sQuery(id+"F0.wireOp",EDGE,"E20.filletArc"),sQuery(id+"F0.wireOp",EDGE,"E25.0"),sQuery(id+"F0.wireOp",EDGE,"E25.1"),sQuery(id+"F0.wireOp",EDGE,"E25.2"),sQuery(id+"F0.wireOp",EDGE,"E25.3"),sQuery(id+"F0.wireOp",EDGE,"E25.4"),sQuery(id+"F0.wireOp",EDGE,"E25.5"),sQuery(id+"F0.wireOp",EDGE,"E25.6"),sQuery(id+"F0.wireOp",EDGE,"E25.7")])],"isStart":false});
            extrude(context, id + "F17", {"entities" : qUnion([Q0, Q1]), "endBound" : BoundingType.UP_TO_SURFACE, "endBoundEntityFace" : qUnion([Q2]), "depth" : 25 * mm});
        }
        {
            var Q0;
            Q0=makeQuery(id+"F16.imprint","IMPRINT",FACE,{"disambiguationData":[TD([[makeQuery(id+"F16.imprint","IMPRINT",EDGE,{"derivedFrom":makeQuery(id+"F1.opExtrude","CAP_EDGE",EDGE,{"disambiguationData":[OSD([sQuery(id+"F0.wireOp",EDGE,"E1.left")])],"isStart":true})}),-1.0]])]});
            var Q1;
            Q1=makeQuery(id+"F2.opExtrude","CAP_FACE",FACE,{"disambiguationData":[OSD([sQuery(id+"F0.wireOp",EDGE,"E12"),sQuery(id+"F0.wireOp",EDGE,"E13"),sQuery(id+"F0.wireOp",EDGE,"E14"),sQuery(id+"F0.wireOp",EDGE,"E15"),sQuery(id+"F0.wireOp",EDGE,"E17.filletArc"),sQuery(id+"F0.wireOp",EDGE,"E18.filletArc"),sQuery(id+"F0.wireOp",EDGE,"E19.filletArc"),sQuery(id+"F0.wireOp",EDGE,"E20.filletArc"),sQuery(id+"F0.wireOp",EDGE,"E25.0"),sQuery(id+"F0.wireOp",EDGE,"E25.1"),sQuery(id+"F0.wireOp",EDGE,"E25.2"),sQuery(id+"F0.wireOp",EDGE,"E25.3"),sQuery(id+"F0.wireOp",EDGE,"E25.4"),sQuery(id+"F0.wireOp",EDGE,"E25.5"),sQuery(id+"F0.wireOp",EDGE,"E25.6"),sQuery(id+"F0.wireOp",EDGE,"E25.7")])],"isStart":false});
            extrude(context, id + "F18", {"entities" : qUnion([Q0]), "endBound" : BoundingType.UP_TO_SURFACE, "endBoundEntityFace" : qUnion([Q1]), "depth" : 25 * mm});
        }
    });
